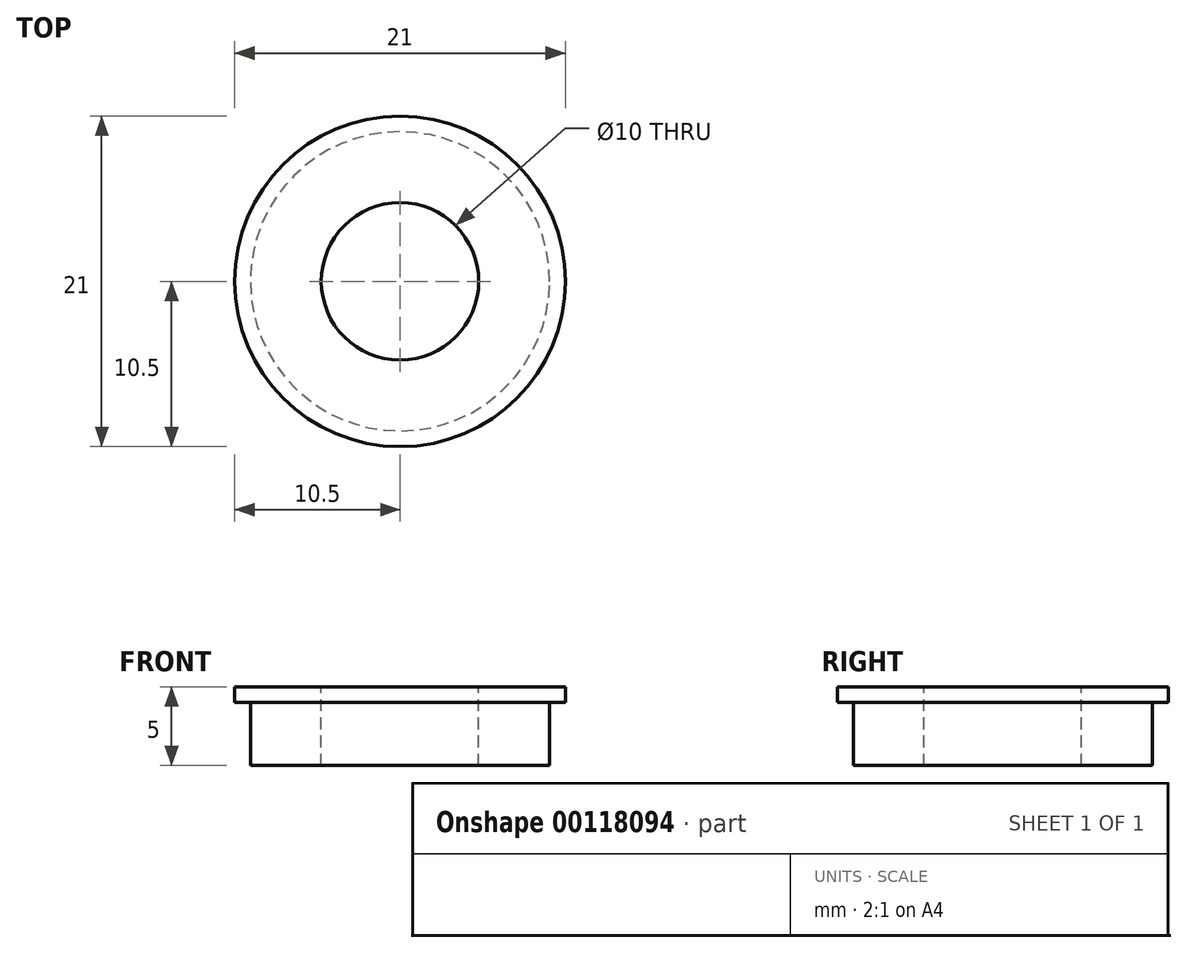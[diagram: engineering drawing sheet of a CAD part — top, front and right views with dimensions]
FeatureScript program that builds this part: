
annotation { "Feature Type Name" : "Feature", "Feature Type Description" : "" }
export const myFeature = defineFeature(function(context is Context, id is Id, definition is map)
    precondition{}
    {
        {
            var Q0;
            Q0=qCreatedBy(makeId("Right.planeOp"),FACE);
            var sketch = newSketch(context, id + "F0", { "sketchPlane" : qUnion([Q0])});
            skLineSegment(sketch, "E0", {"start": v(0, 0) * mm, "end": v(-5, 0) * mm, "construction": true});
            skLineSegment(sketch, "E1", {"start": v(-5, 0) * mm, "end": v(-10.5, 0) * mm});
            skLineSegment(sketch, "E2", {"start": v(-10.5, 0) * mm, "end": v(-10.5, -1) * mm});
            skLineSegment(sketch, "E3", {"start": v(-10.5, -1) * mm, "end": v(-9.5, -1) * mm});
            skLineSegment(sketch, "E4", {"start": v(-9.5, -1) * mm, "end": v(-9.5, -5) * mm});
            skLineSegment(sketch, "E5", {"start": v(-9.5, -5) * mm, "end": v(-5, -5) * mm});
            skLineSegment(sketch, "E6", {"start": v(-5, -5) * mm, "end": v(-5, 0) * mm});
            skLineSegment(sketch, "E7", {"start": v(0, 0) * mm, "end": v(0, -8.92) * mm, "construction": true});
            skSolve(sketch);
        }
        {
            var Q0;
            Q0=makeQuery(id+"F0.imprint","IMPRINT",FACE,{"disambiguationData":[TD([[makeQuery(id+"F0.imprint","IMPRINT",EDGE,{"derivedFrom":sQuery(id+"F0.wireOp",EDGE,"E1")}),1.0]])]});
            var Q1;
            Q1=sQuery(id+"F0.wireOp",EDGE,"E7");
            revolve(context, id + "F1", {"entities" : qUnion([Q0]), "axis" : qUnion([Q1]), "revolveType" : RevolveType.FULL});
        }
    });
